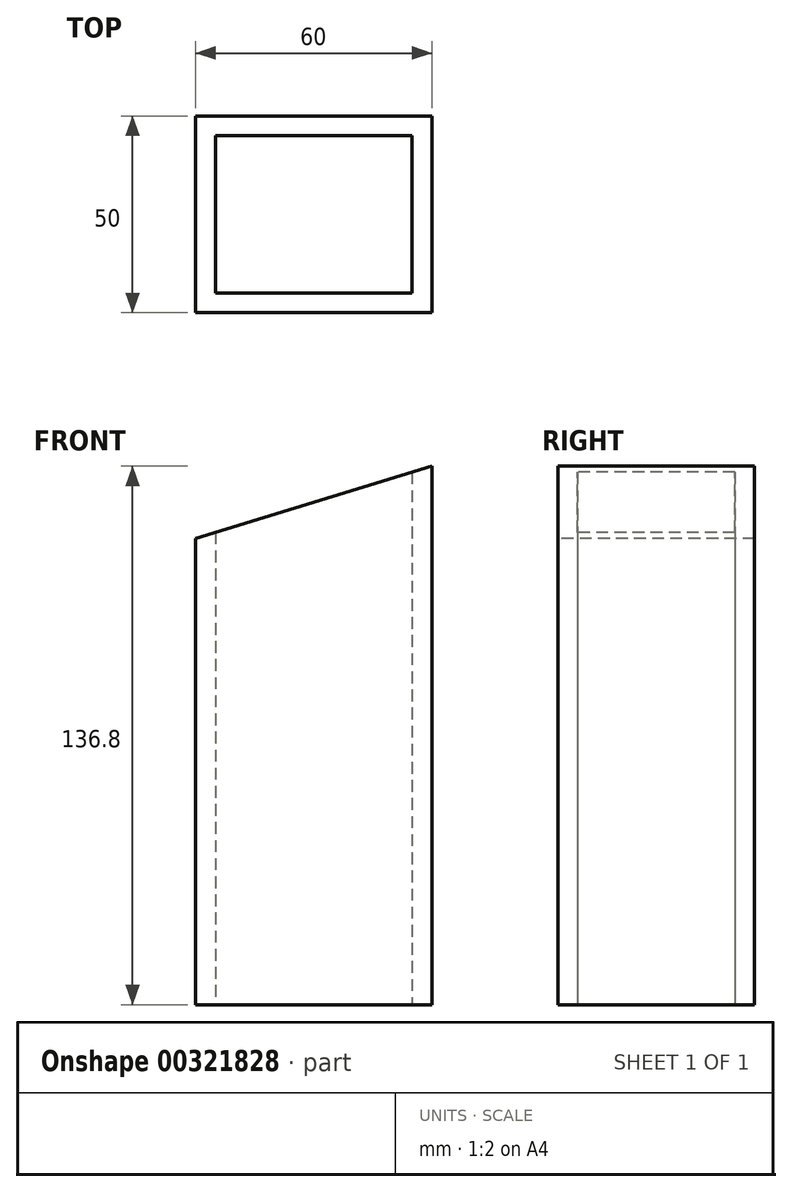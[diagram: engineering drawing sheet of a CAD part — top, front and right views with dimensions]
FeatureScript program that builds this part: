
annotation { "Feature Type Name" : "Feature", "Feature Type Description" : "" }
export const myFeature = defineFeature(function(context is Context, id is Id, definition is map)
    precondition{}
    {
        {
            var Q0;
            Q0=qCreatedBy(makeId("Top.planeOp"),FACE);
            var sketch = newSketch(context, id + "F0", { "sketchPlane" : qUnion([Q0])});
            skLineSegment(sketch, "E0.bottom", {"start": v(-30, 25) * mm, "end": v(30, 25) * mm});
            skLineSegment(sketch, "E0.top", {"start": v(-30, -25) * mm, "end": v(30, -25) * mm});
            skLineSegment(sketch, "E0.left", {"start": v(-30, 25) * mm, "end": v(-30, -25) * mm});
            skLineSegment(sketch, "E0.right", {"start": v(30, 25) * mm, "end": v(30, -25) * mm});
            skLineSegment(sketch, "E1.0", {"start": v(-25, 20) * mm, "end": v(25, 20) * mm});
            skLineSegment(sketch, "E1.1", {"start": v(-25, 20) * mm, "end": v(-25, -20) * mm});
            skLineSegment(sketch, "E1.2", {"start": v(-25, -20) * mm, "end": v(25, -20) * mm});
            skLineSegment(sketch, "E1.3", {"start": v(25, 20) * mm, "end": v(25, -20) * mm});
            skSolve(sketch);
        }
        {
            var Q0;
            Q0=makeQuery(id+"F0.imprint","IMPRINT",FACE,{"disambiguationData":[TD([[makeQuery(id+"F0.imprint","IMPRINT",EDGE,{"derivedFrom":sQuery(id+"F0.wireOp",EDGE,"E0.bottom")}),-1.0]])]});
            extrude(context, id + "F1", {"entities" : qUnion([Q0]), "depth" : 136.8 * mm});
        }
        {
            var Q0;
            Q0=makeQuery(id+"F1.opExtrude","SWEPT_FACE",FACE,{"disambiguationData":[OSD([sQuery(id+"F0.wireOp",EDGE,"E0.top")])]});
            var sketch = newSketch(context, id + "F2", { "sketchPlane" : qUnion([Q0])});
            skLineSegment(sketch, "E2.0", {"start": v(-30, 136.8) * mm, "end": v(30, 136.8) * mm});
            skLineSegment(sketch, "E3", {"start": v(30, 136.8) * mm, "end": v(-30, 118.46) * mm});
            skLineSegment(sketch, "E4", {"start": v(-30, 136.8) * mm, "end": v(-30, 118.46) * mm});
            skSolve(sketch);
        }
        {
            var Q0;
            Q0=makeQuery(id+"F2.imprint","IMPRINT",FACE,{"disambiguationData":[TD([[makeQuery(id+"F2.imprint","IMPRINT",EDGE,{"derivedFrom":sQuery(id+"F2.wireOp",EDGE,"E2.0")}),-1.0]])]});
            extrude(context, id + "F3", {"entities" : qUnion([Q0]), "operationType" : NewBodyOperationType.REMOVE, "oppositeDirection" : true, "depth" : 60 * mm});
        }
    });
